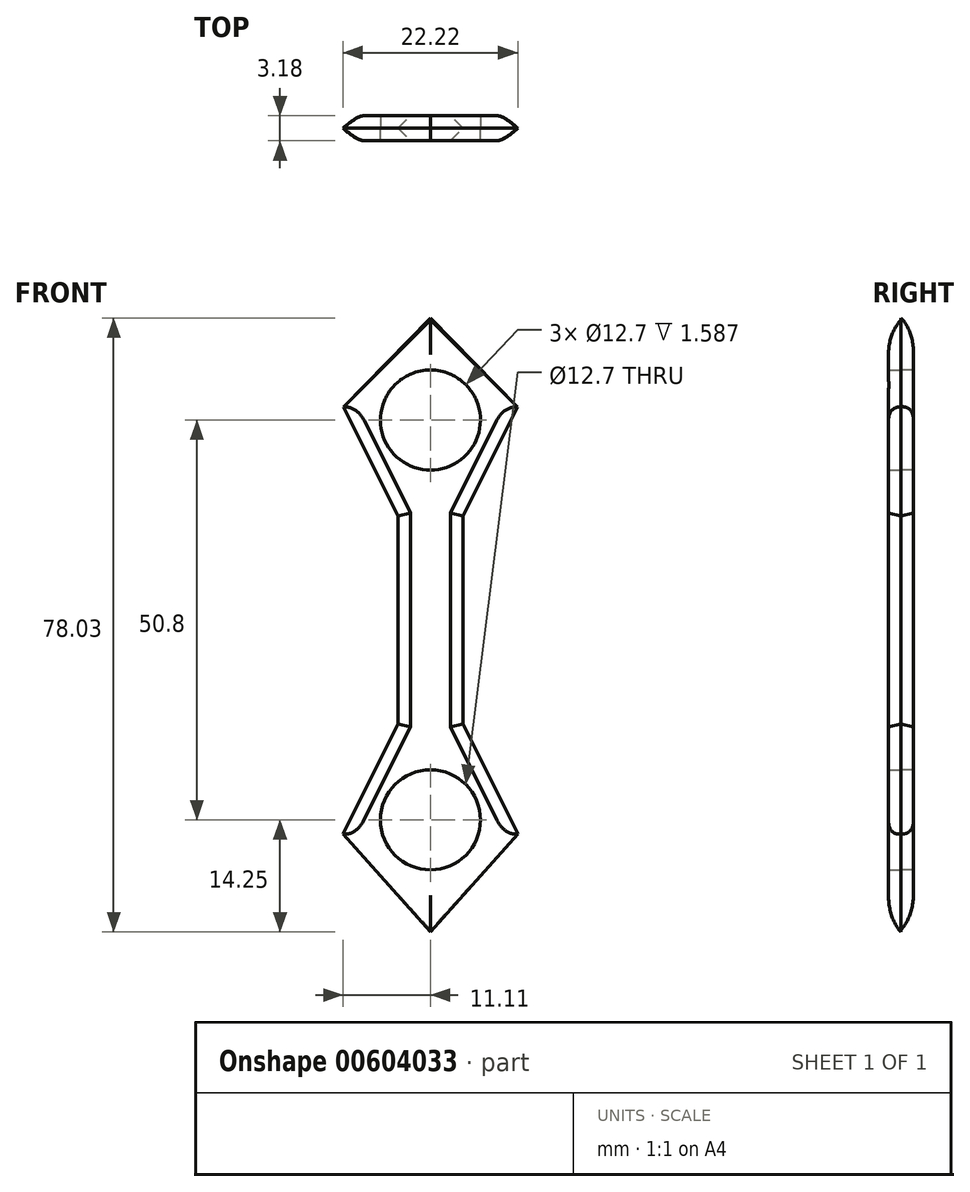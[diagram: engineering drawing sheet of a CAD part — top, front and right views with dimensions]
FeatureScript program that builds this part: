
annotation { "Feature Type Name" : "Feature", "Feature Type Description" : "" }
export const myFeature = defineFeature(function(context is Context, id is Id, definition is map)
    precondition{}
    {
        {
            var Q0;
            Q0=qCreatedBy(makeId("Front.planeOp"),FACE);
            var sketch = newSketch(context, id + "F0", { "sketchPlane" : qUnion([Q0])});
            skCircle(sketch, "E0", {"center": v(0, 0) * mm, "radius": 6.35 * mm});
            skLineSegment(sketch, "E1", {"start": v(0, 0) * mm, "end": v(0, 50.8) * mm, "construction": true});
            skCircle(sketch, "E2", {"center": v(0, 50.8) * mm, "radius": 6.35 * mm});
            skLineSegment(sketch, "E3", {"start": v(0, 50.8) * mm, "end": v(0, 25.4) * mm, "construction": true});
            skLineSegment(sketch, "E4", {"start": v(0, 25.4) * mm, "end": v(0, 12.7) * mm, "construction": true});
            skLineSegment(sketch, "E5", {"start": v(0, 25.4) * mm, "end": v(0, 38.1) * mm, "construction": true});
            skLineSegment(sketch, "E6", {"start": v(0, -14.25) * mm, "end": v(12.7, 0) * mm});
            skLineSegment(sketch, "E7", {"start": v(12.7, 0) * mm, "end": v(6.35, 12.7) * mm});
            skLineSegment(sketch, "E8", {"start": v(6.35, 12.7) * mm, "end": v(6.35, 25.4) * mm});
            skLineSegment(sketch, "E9", {"start": v(-12.7, 0) * mm, "end": v(0, -14.25) * mm});
            skLineSegment(sketch, "E10", {"start": v(6.35, 25.4) * mm, "end": v(6.35, 38.1) * mm});
            skLineSegment(sketch, "E11", {"start": v(-12.7, 0) * mm, "end": v(-6.35, 12.7) * mm});
            skLineSegment(sketch, "E12", {"start": v(-6.35, 12.7) * mm, "end": v(-6.35, 38.1) * mm});
            skLineSegment(sketch, "E13", {"start": v(-6.35, 38.1) * mm, "end": v(-12.7, 50.8) * mm});
            skLineSegment(sketch, "E14", {"start": v(-12.7, 50.8) * mm, "end": v(0, 63.5) * mm});
            skLineSegment(sketch, "E15", {"start": v(12.7, 50.8) * mm, "end": v(0, 63.5) * mm});
            skLineSegment(sketch, "E16", {"start": v(6.35, 38.1) * mm, "end": v(12.7, 50.8) * mm});
            skLineSegment(sketch, "E17", {"start": v(0, -14.25) * mm, "end": v(0, 63.5) * mm, "construction": true});
            skLineSegment(sketch, "E18", {"start": v(6.35, 25.4) * mm, "end": v(0, 25.4) * mm, "construction": true});
            skSolve(sketch);
        }
        {
            var Q0;
            Q0=makeQuery(id+"F0.imprint","IMPRINT",FACE,{"disambiguationData":[TD([[makeQuery(id+"F0.imprint","IMPRINT",EDGE,{"derivedFrom":sQuery(id+"F0.wireOp",EDGE,"E0")}),-1.0]])]});
            extrude(context, id + "F1", {"entities" : qUnion([Q0]), "depth" : 1.59 * mm, "offsetDistance" : 25.4 * mm});
        }
        {
            var Q0;
            Q0=qCreatedBy(makeId("Front.planeOp"),FACE);
            var sketch = newSketch(context, id + "F2", { "sketchPlane" : qUnion([Q0])});
            skLineSegment(sketch, "E19", {"start": v(0, 0) * mm, "end": v(-12.7, 0) * mm, "construction": true});
            skLineSegment(sketch, "E20", {"start": v(0, 0) * mm, "end": v(0, -13.97) * mm, "construction": true});
            skLineSegment(sketch, "E21", {"start": v(0, 0) * mm, "end": v(12.7, 0) * mm, "construction": true});
            skLineSegment(sketch, "E22", {"start": v(0, -13.97) * mm, "end": v(0, 63.78) * mm, "construction": true});
            skLineSegment(sketch, "E23", {"start": v(0, 0) * mm, "end": v(0, 50.8) * mm, "construction": true});
            skCircle(sketch, "E24", {"center": v(0, 50.8) * mm, "radius": 6.35 * mm});
            skLineSegment(sketch, "E25", {"start": v(0, 50.8) * mm, "end": v(12.7, 50.8) * mm, "construction": true});
            skLineSegment(sketch, "E26", {"start": v(0, 50.8) * mm, "end": v(-12.7, 50.8) * mm, "construction": true});
            skLineSegment(sketch, "E27", {"start": v(0, 50.8) * mm, "end": v(0, 25.4) * mm, "construction": true});
            skLineSegment(sketch, "E28", {"start": v(0, 25.4) * mm, "end": v(6.35, 25.4) * mm, "construction": true});
            skLineSegment(sketch, "E29", {"start": v(0, 25.4) * mm, "end": v(-6.35, 25.4) * mm, "construction": true});
            skLineSegment(sketch, "E30", {"start": v(6.35, 25.4) * mm, "end": v(6.35, 38.1) * mm, "construction": true});
            skLineSegment(sketch, "E31", {"start": v(6.35, 25.4) * mm, "end": v(6.35, 12.7) * mm, "construction": true});
            skLineSegment(sketch, "E32", {"start": v(6.35, 12.7) * mm, "end": v(-6.35, 12.7) * mm, "construction": true});
            skLineSegment(sketch, "E33", {"start": v(6.35, 38.1) * mm, "end": v(-6.35, 38.1) * mm, "construction": true});
            skPoint(sketch, "E33.endSnap0", {"position": v(0, 38.1) * mm});
            skLineSegment(sketch, "E34", {"start": v(12.7, 0) * mm, "end": v(0, -13.97) * mm});
            skLineSegment(sketch, "E35", {"start": v(0, -13.97) * mm, "end": v(-12.7, 0) * mm});
            skLineSegment(sketch, "E36", {"start": v(-12.7, 0) * mm, "end": v(-6.35, 12.7) * mm});
            skLineSegment(sketch, "E37", {"start": v(-6.35, 12.7) * mm, "end": v(-6.35, 25.4) * mm});
            skLineSegment(sketch, "E38", {"start": v(-6.35, 25.4) * mm, "end": v(-6.35, 38.1) * mm});
            skLineSegment(sketch, "E39", {"start": v(-6.35, 38.1) * mm, "end": v(-12.7, 50.8) * mm});
            skLineSegment(sketch, "E40", {"start": v(-12.7, 50.8) * mm, "end": v(0, 63.78) * mm});
            skLineSegment(sketch, "E41", {"start": v(0, 63.78) * mm, "end": v(12.7, 50.8) * mm});
            skLineSegment(sketch, "E42", {"start": v(12.7, 50.8) * mm, "end": v(6.35, 38.1) * mm});
            skLineSegment(sketch, "E43", {"start": v(6.35, 38.1) * mm, "end": v(6.35, 25.4) * mm});
            skLineSegment(sketch, "E44", {"start": v(6.35, 25.4) * mm, "end": v(6.35, 12.7) * mm});
            skLineSegment(sketch, "E45", {"start": v(6.35, 12.7) * mm, "end": v(12.7, 0) * mm});
            skCircle(sketch, "E46", {"center": v(0, 0) * mm, "radius": 6.35 * mm});
            skSolve(sketch);
        }
        {
            var Q0;
            Q0 = qSketchRegion(id + "F2", true);
            extrude(context, id + "F3", {"entities" : qUnion([Q0]), "depth" : -1.59 * mm, "offsetDistance" : 25.4 * mm});
        }
        {
            var Q0;
            Q0=makeQuery(id+"F1.opExtrude","CAP_EDGE",EDGE,{"disambiguationData":[OSD([sQuery(id+"F0.wireOp",EDGE,"E8"),sQuery(id+"F0.wireOp",EDGE,"E10")])],"isStart":false});
            var Q1;
            Q1=makeQuery(id+"F3.opExtrude","CAP_EDGE",EDGE,{"disambiguationData":[OSD([sQuery(id+"F2.wireOp",EDGE,"E43"),sQuery(id+"F2.wireOp",EDGE,"E44")])],"isStart":false});
            var Q2;
            Q2=makeQuery(id+"F3.opExtrude","CAP_EDGE",EDGE,{"disambiguationData":[OSD([sQuery(id+"F2.wireOp",EDGE,"E37"),sQuery(id+"F2.wireOp",EDGE,"E38")])],"isStart":false});
            var Q3;
            Q3=makeQuery(id+"F1.opExtrude","CAP_EDGE",EDGE,{"disambiguationData":[OSD([sQuery(id+"F0.wireOp",EDGE,"E12")])],"isStart":false});
            var Q4;
            Q4=makeQuery(id+"F1.opExtrude","CAP_EDGE",EDGE,{"disambiguationData":[OSD([sQuery(id+"F0.wireOp",EDGE,"E16")])],"isStart":false});
            var Q5;
            Q5=makeQuery(id+"F1.opExtrude","CAP_EDGE",EDGE,{"disambiguationData":[OSD([sQuery(id+"F0.wireOp",EDGE,"E13")])],"isStart":false});
            var Q6;
            Q6=makeQuery(id+"F1.opExtrude","CAP_EDGE",EDGE,{"disambiguationData":[OSD([sQuery(id+"F0.wireOp",EDGE,"E7")])],"isStart":false});
            var Q7;
            Q7=makeQuery(id+"F1.opExtrude","CAP_EDGE",EDGE,{"disambiguationData":[OSD([sQuery(id+"F0.wireOp",EDGE,"E11")])],"isStart":false});
            var Q8;
            Q8=makeQuery(id+"F3.opExtrude","CAP_EDGE",EDGE,{"disambiguationData":[OSD([sQuery(id+"F2.wireOp",EDGE,"E36")])],"isStart":false});
            var Q9;
            Q9=makeQuery(id+"F3.opExtrude","CAP_EDGE",EDGE,{"disambiguationData":[OSD([sQuery(id+"F2.wireOp",EDGE,"E45")])],"isStart":false});
            var Q10;
            Q10=makeQuery(id+"F3.opExtrude","CAP_EDGE",EDGE,{"disambiguationData":[OSD([sQuery(id+"F2.wireOp",EDGE,"E39")])],"isStart":false});
            var Q11;
            Q11=makeQuery(id+"F3.opExtrude","CAP_EDGE",EDGE,{"disambiguationData":[OSD([sQuery(id+"F2.wireOp",EDGE,"E42")])],"isStart":false});
            chamfer(context, id + "F4", {"entities" : qUnion([Q0, Q1, Q2, Q3, Q4, Q5, Q6, Q7, Q8, Q9, Q10, Q11]), "width" : 3.8 * mm, "tangentPropagation" : true});
        }
        {
            var Q0;
            Q0=makeQuery(id+"F3.opExtrude","CAP_EDGE",EDGE,{"disambiguationData":[OSD([sQuery(id+"F2.wireOp",EDGE,"E35")])],"isStart":false});
            var Q1;
            Q1=makeQuery(id+"F1.opExtrude","CAP_EDGE",EDGE,{"disambiguationData":[OSD([sQuery(id+"F0.wireOp",EDGE,"E6")])],"isStart":false});
            var Q2;
            Q2=makeQuery(id+"F1.opExtrude","CAP_EDGE",EDGE,{"disambiguationData":[OSD([sQuery(id+"F0.wireOp",EDGE,"E9")])],"isStart":false});
            var Q3;
            Q3=makeQuery(id+"F3.opExtrude","CAP_EDGE",EDGE,{"disambiguationData":[OSD([sQuery(id+"F2.wireOp",EDGE,"E34")])],"isStart":false});
            var Q4;
            Q4=makeQuery(id+"F1.opExtrude","CAP_EDGE",EDGE,{"disambiguationData":[OSD([sQuery(id+"F0.wireOp",EDGE,"E15")])],"isStart":false});
            var Q5;
            Q5=makeQuery(id+"F3.opExtrude","CAP_EDGE",EDGE,{"disambiguationData":[OSD([sQuery(id+"F2.wireOp",EDGE,"E41")])],"isStart":false});
            var Q6;
            Q6=makeQuery(id+"F3.opExtrude","CAP_EDGE",EDGE,{"disambiguationData":[OSD([sQuery(id+"F2.wireOp",EDGE,"E40")])],"isStart":false});
            var Q7;
            Q7=makeQuery(id+"F1.opExtrude","CAP_EDGE",EDGE,{"disambiguationData":[OSD([sQuery(id+"F0.wireOp",EDGE,"E14")])],"isStart":false});
            fillet(context, id + "F5", {"entities" : qUnion([Q0, Q1, Q2, Q3, Q4, Q5, Q6, Q7]), "radius" : 3.8 * mm, "tangentPropagation" : true, "allowEdgeOverflow" : false});
        }
    });
